# Revit family: PGR_Noken_ShwrHdHldrs_BRAZO_ROCIADOR_RONDO
name_source: partatom
category: Plumbing Fixtures
revit_build: Autodesk Revit 2017 (Build: 20190508_0315(x64)
units: mm (PartAtom-declared; Revit-internal decimal feet)

## family parameters
Always vertical = Yes
Cut with Voids When Loaded = No
OmniClass Number = 23.45.55.17
OmniClass Title = Mixing Faucets
Part Type = Normal
Room Calculation Point = No
Round Connector Dimension = Use Diameter
Shared = No
Work Plane-Based = No

## types (1)
- BRAZO ROCIADOR CROMO - 100090331
    AccessibilityPerformance = See ProductInformation for technical PDF
    AssetType = Fixed
    BIMObjectName = PGR_Noken_ShowerHeads_RONDO_chrome-200x30x30mm-100090331
    Category = Pr_40_20_87_76: Shower heads
    Collection = RONDO
    Color = Chrome
    Constituents = Shower head arm
    DrainSize = 0 mm
    DurationUnit = Year
    Features = See ProductInformation for technical PDF
    Finish = chrome
    HasTray = No
    IfcExportAs = IfcSanitaryTerminalType
    IfcExportType = Shower
    ManufacturerURL = www.noken.com
    Material = Brass
    MaterialMetal = PGR_Noken_Brass_Chrome
    MaterialThickness = 0 mm  [stored 0 ft]
    Model = 100090331
    ModelNumber = 100090331
    ModelReference = BRAZO ROCIADOR RONDO VERTICAL 20CM CROMO
    NBSDescription = Shower Heads
    NBSReference = 45-35-70/333
    Name = ShowerHeads_RONDO_chrome-200x30x30mm-100090331
    NettWeight = 0
    NominalDepth = 0 mm  [stored 0 ft]
    NominalHeight = 200 mm  [stored 0.656168 ft]
    NominalLength = 60 mm  [stored 0.19685 ft]
    NominalWidth = 60 mm  [stored 0.19685 ft]
    ProductInformation = http://calidad.info-grupo.com:8081
    Reference = -
    Shape = Round
    ShowerHeadDescription = Rondo. Shower arm. Material brass, finish chrome plated, nominal lenght 200, nominal height 30, nominal width30, net product weight 0,3. UNE EN 1112, UNE EN 248
    ShowerType = UNSET
    Size = 200x30x30mm
    Status = UNSET
    SustainabilityPerformance = See ProductInformation for technical PDF
    TechnicalDrawing = See ProductInformation for technical PDF
    Type Image = 100090331.jpg
    URL = www.noken.com
    Uniclass2015Code = Pr_40_20_87_76
    Uniclass2015Title = Shower heads
    Uniclass2015Version = V1_9
    Version = 1
    WarrantyDescription = See ProductInformation for technical PDF
    WarrantyDurationUnit = Year

note: [stored X ft] marks values corroborated as IEEE doubles in the binary element streams (Revit-internal decimal feet)

## geometry (parser evidence)
native form markers: Blend x2, Sweep x2
no freeform markers — native parametric forms only
